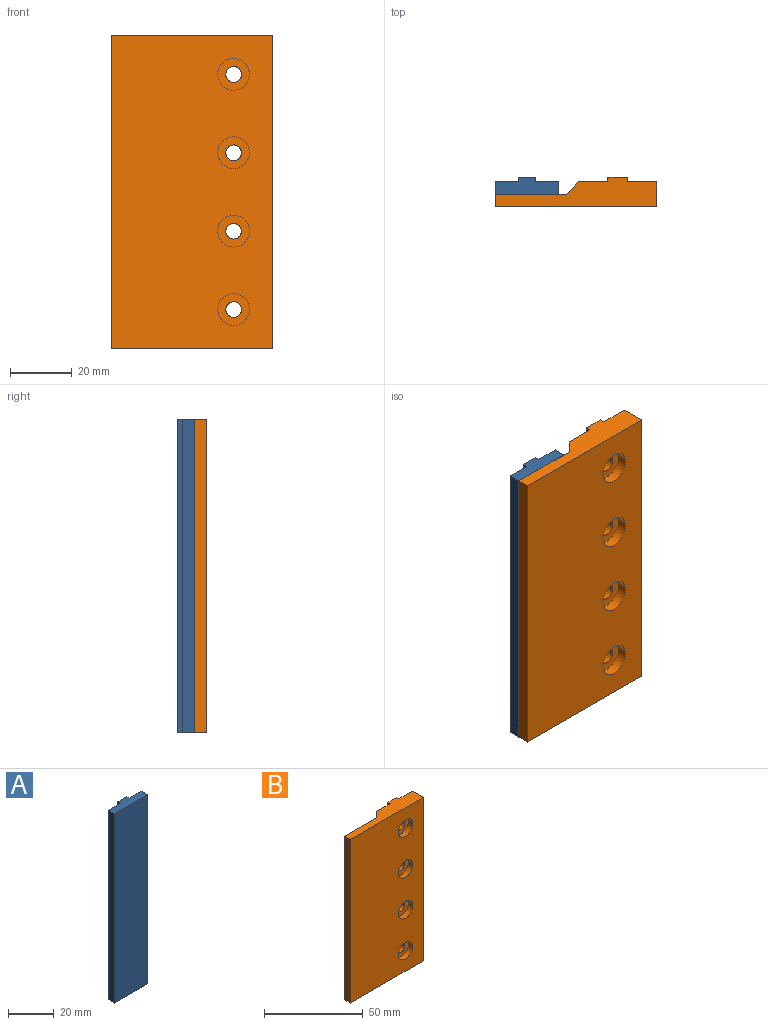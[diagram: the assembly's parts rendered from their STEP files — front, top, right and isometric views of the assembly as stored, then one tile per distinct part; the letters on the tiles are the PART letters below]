
ASSEMBLY  parts=2 mates=1
PART A: 10 faces, bbox 20.6x5.6x101.6 mm
  f0: plane 101.6x3.97mm, normal (-1,0,0), area 403.2mm2, adj f1,f7,f8,f9
  f1: plane 101.6x20.64mm, normal (0,-1,0), area 2096.8mm2, adj f0,f2,f8,f9
  f2: plane 101.6x3.97mm, normal (1,0,0), area 403.2mm2, adj f1,f3,f8,f9
  f3: plane 101.6x7.54mm, normal (0,1,0), area 766.1mm2, adj f2,f4,f8,f9
  f4: plane 101.6x1.59mm, normal (1,0,0), area 161.3mm2, adj f3,f5,f8,f9
  f5: plane 101.6x5.56mm, normal (0,1,0), area 564.5mm2, adj f4,f6,f8,f9
  f6: plane 101.6x1.59mm, normal (-1,0,0), area 161.3mm2, adj f5,f7,f8,f9
  f7: plane 101.6x7.54mm, normal (0,1,0), area 766.1mm2, adj f0,f6,f8,f9
  f8: plane 20.64x5.56mm, normal (0,0,-1), area 90.7mm2, adj f0,f1,f2,f3,f4,f5,f6,f7
  f9: plane 20.64x5.56mm, normal (0,0,1), area 90.7mm2, adj f0,f1,f2,f3,f4,f5,f6,f7
PART B: 24 faces, bbox 52.4x9.5x101.6 mm
  f0: plane 101.6x7.94mm, normal (1,0,0), area 806.5mm2, adj f1,f9,f10,f11
  f1: plane 101.6x52.39mm, normal (0,-1,0), area 4988.1mm2, adj f0,f2,f10,f11,f12,f14,f16,f18
  f2: plane 101.6x3.97mm, normal (-1,0,0), area 403.2mm2, adj f1,f3,f10,f11
  f3: plane 101.6x23.02mm, normal (0,1,0), area 2338.7mm2, adj f2,f4,f10,f11
  f4: plane 101.6x3.97mm, normal (-0.71,0.71,0), area 570.2mm2, adj f3,f5,f10,f11
  f5: plane 101.6x9.53mm, normal (0,1,0), area 967.7mm2, adj f4,f6,f10,f11
  f6: plane 101.6x1.59mm, normal (-1,0,0), area 161.3mm2, adj f5,f7,f10,f11
  f7: plane 101.6x6.35mm, normal (0,1,0), area 564.1mm2, adj f6,f8,f10,f11,f20,f21,f22,f23
  f8: plane 101.6x1.59mm, normal (1,0,0), area 161.3mm2, adj f7,f9,f10,f11
  f9: plane 101.6x9.53mm, normal (0,1,0), area 967.7mm2, adj f0,f8,f10,f11
  f10: plane 52.39x9.53mm, normal (0,0,1), area 326.7mm2, adj f0,f1,f2,f3,f4,f5,f6,f7
  f11: plane 52.39x9.53mm, normal (0,0,-1), area 326.7mm2, adj f0,f1,f2,f3,f4,f5,f6,f7
  f12: cylinder r=5.16mm len=10.32mm, axis (0,-1,0), area 102.9mm2, adj f1,f13
  f13: plane 10.32x10.32mm, normal (0,-1,0), area 63.4mm2, adj f12,f23
  f14: cylinder r=5.16mm len=10.32mm, axis (0,-1,0), area 102.9mm2, adj f1,f15
  f15: plane 10.32x10.32mm, normal (0,-1,0), area 63.4mm2, adj f14,f22
  f16: cylinder r=5.16mm len=10.32mm, axis (0,-1,0), area 102.9mm2, adj f1,f17
  f17: plane 10.32x10.32mm, normal (0,-1,0), area 63.4mm2, adj f16,f21
  f18: cylinder r=5.16mm len=10.32mm, axis (0,-1,0), area 102.9mm2, adj f1,f19
  f19: plane 10.32x10.32mm, normal (0,-1,0), area 63.4mm2, adj f18,f20
  f20: cylinder r=2.54mm len=6.35mm, axis (0,-1,0), area 101.3mm2, adj f7,f19
  f21: cylinder r=2.54mm len=6.35mm, axis (0,-1,0), area 101.3mm2, adj f7,f17
  f22: cylinder r=2.54mm len=6.35mm, axis (0,-1,0), area 101.3mm2, adj f7,f15
  f23: cylinder r=2.54mm len=6.35mm, axis (0,-1,0), area 101.3mm2, adj f7,f13
PLACE A t=(-78.98,-3.88,-31.25)mm
PLACE B t=(-99.62,-3.88,-31.25)mm
MATE fastened A.f1 <-> B.f3  axis (0,-1,0) through (-47.23,0.09,70.35)mm
